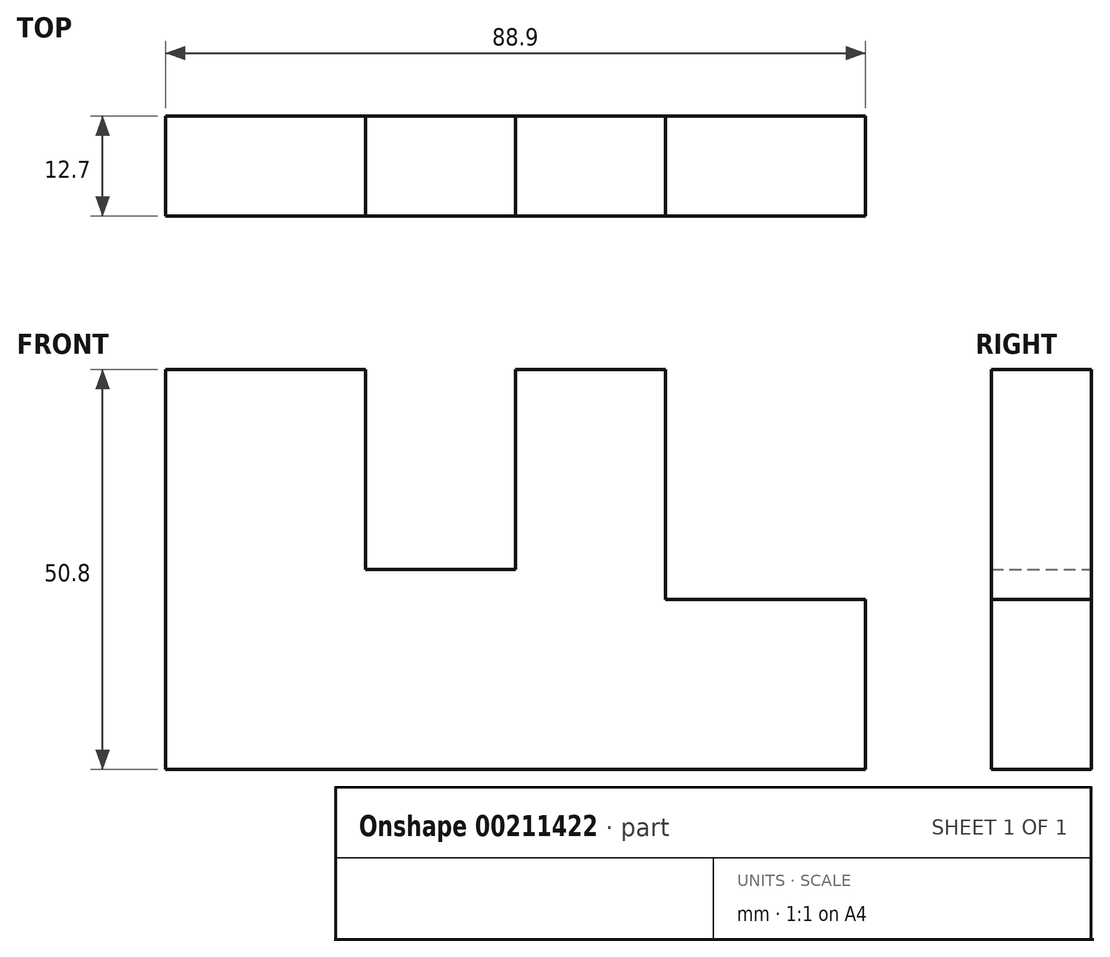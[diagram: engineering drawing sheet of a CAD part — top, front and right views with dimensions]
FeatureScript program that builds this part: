
annotation { "Feature Type Name" : "Feature", "Feature Type Description" : "" }
export const myFeature = defineFeature(function(context is Context, id is Id, definition is map)
    precondition{}
    {
        {
            var Q0;
            Q0=qCreatedBy(makeId("Front.planeOp"),FACE);
            var sketch = newSketch(context, id + "F0", { "sketchPlane" : qUnion([Q0])});
            skLineSegment(sketch, "E0", {"start": v(0, 0) * mm, "end": v(0, 50.8) * mm});
            skLineSegment(sketch, "E1", {"start": v(0, 50.8) * mm, "end": v(25.4, 50.8) * mm});
            skLineSegment(sketch, "E2", {"start": v(25.4, 50.8) * mm, "end": v(25.4, 25.4) * mm});
            skLineSegment(sketch, "E3", {"start": v(25.4, 25.4) * mm, "end": v(44.45, 25.4) * mm});
            skLineSegment(sketch, "E4", {"start": v(44.45, 25.4) * mm, "end": v(44.45, 50.8) * mm});
            skLineSegment(sketch, "E5", {"start": v(44.45, 50.8) * mm, "end": v(63.5, 50.8) * mm});
            skLineSegment(sketch, "E6", {"start": v(63.5, 50.8) * mm, "end": v(63.5, 21.6) * mm});
            skLineSegment(sketch, "E7", {"start": v(63.5, 21.6) * mm, "end": v(88.9, 21.6) * mm});
            skLineSegment(sketch, "E8", {"start": v(88.9, 21.6) * mm, "end": v(88.9, 0) * mm});
            skLineSegment(sketch, "E9", {"start": v(88.9, 0) * mm, "end": v(0, 0) * mm});
            skSolve(sketch);
        }
        {
            var Q0;
            Q0=makeQuery(id+"F0.imprint","IMPRINT",FACE,{"disambiguationData":[TD([[makeQuery(id+"F0.imprint","IMPRINT",EDGE,{"derivedFrom":sQuery(id+"F0.wireOp",EDGE,"E0")}),-1.0]])]});
            extrude(context, id + "F1", {"entities" : qUnion([Q0]), "depth" : 12.7 * mm});
        }
    });
